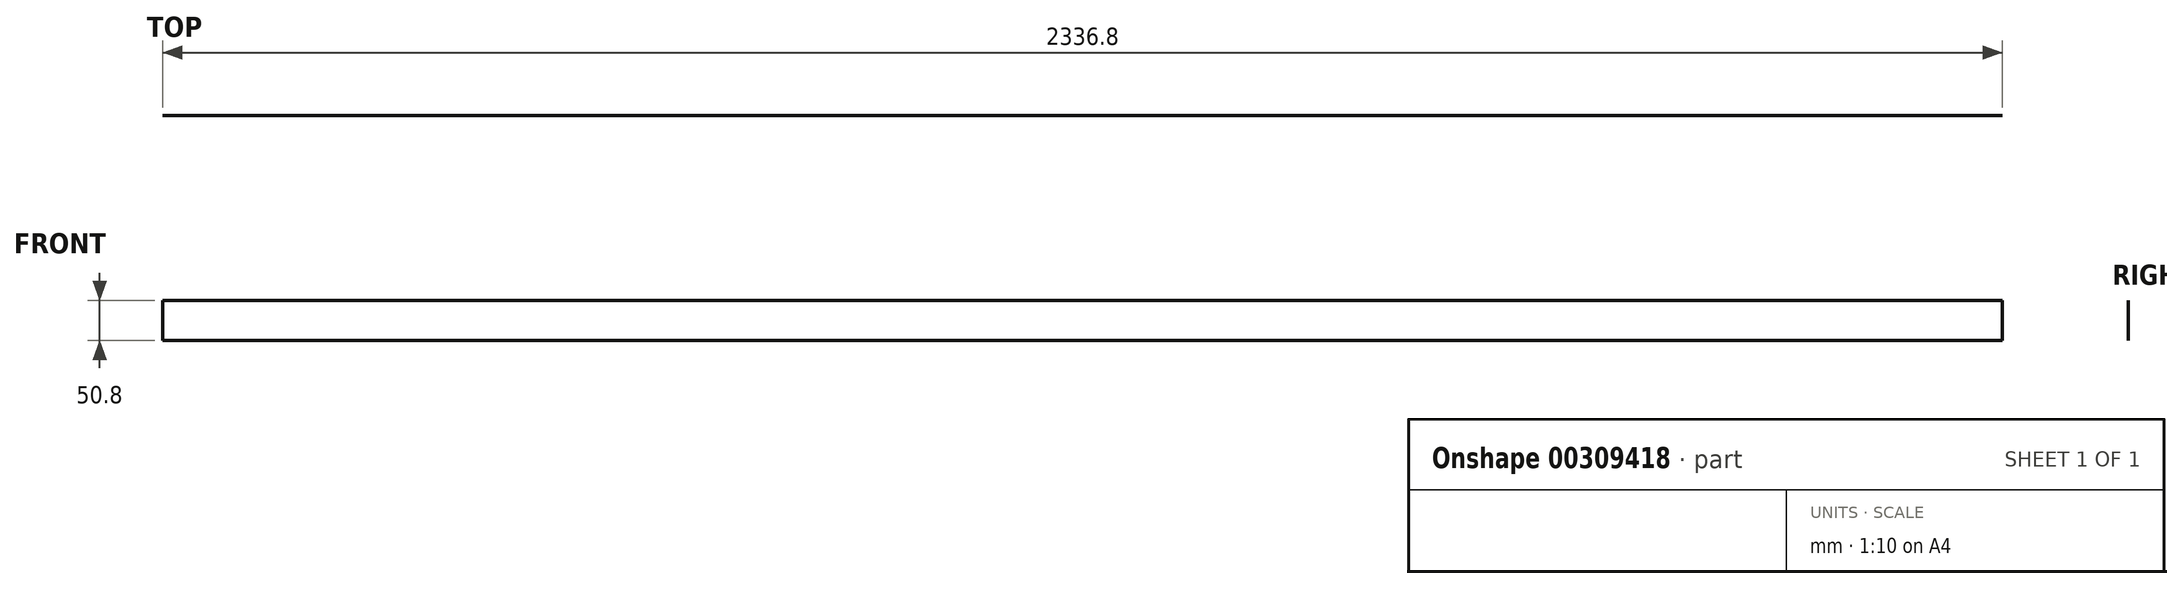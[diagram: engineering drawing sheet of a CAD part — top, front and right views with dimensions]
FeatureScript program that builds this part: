
annotation { "Feature Type Name" : "Feature", "Feature Type Description" : "" }
export const myFeature = defineFeature(function(context is Context, id is Id, definition is map)
    precondition{}
    {
        {
            var Q0;
            Q0=qCreatedBy(makeId("Front.planeOp"),FACE);
            var sketch = newSketch(context, id + "F0", { "sketchPlane" : qUnion([Q0])});
            skLineSegment(sketch, "E0.bottom", {"start": v(-457.88, 37.6) * mm, "end": v(1878.92, 37.6) * mm});
            skLineSegment(sketch, "E0.top", {"start": v(-457.88, -13.2) * mm, "end": v(1878.92, -13.2) * mm});
            skLineSegment(sketch, "E0.left", {"start": v(-457.88, 37.6) * mm, "end": v(-457.88, -13.2) * mm});
            skLineSegment(sketch, "E0.right", {"start": v(1878.92, 37.6) * mm, "end": v(1878.92, -13.2) * mm});
            skSolve(sketch);
        }
        {
            var Q0;
            Q0 = qSketchRegion(id + "F0", true);
            extrude(context, id + "F1", {"entities" : qUnion([Q0]), "depth" : 1 / 203.2 * mm});
        }
    });
